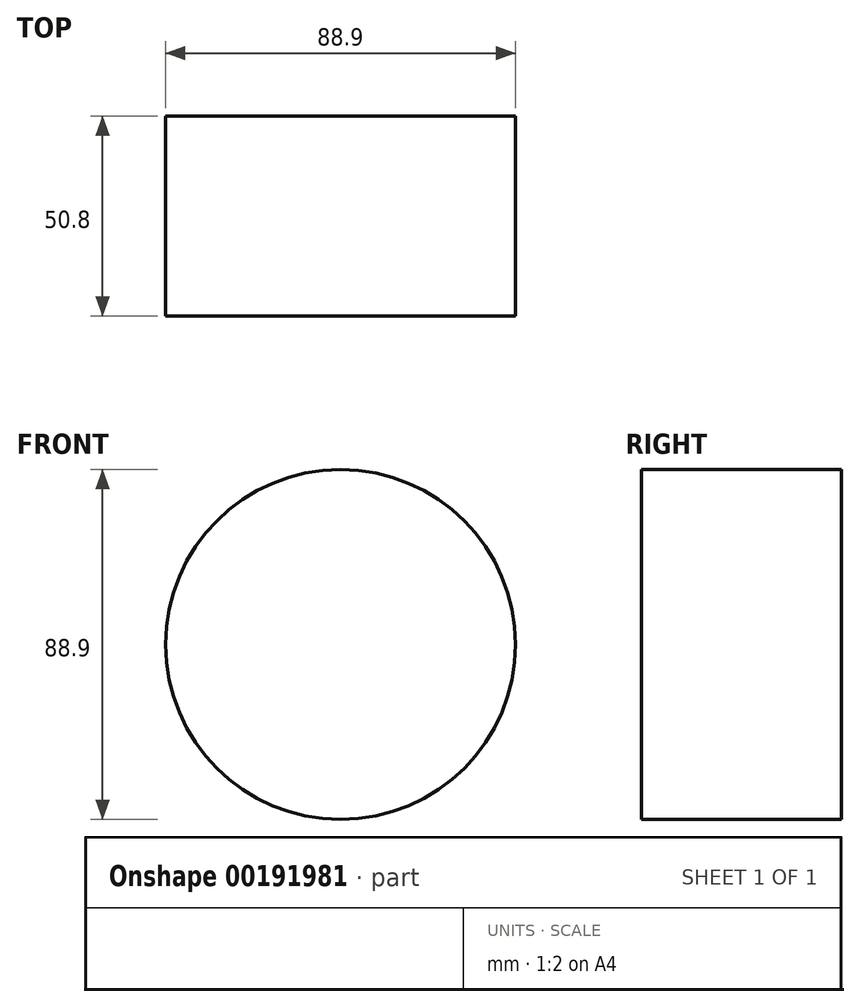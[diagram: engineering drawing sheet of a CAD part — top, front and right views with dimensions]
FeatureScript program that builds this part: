
annotation { "Feature Type Name" : "Feature", "Feature Type Description" : "" }
export const myFeature = defineFeature(function(context is Context, id is Id, definition is map)
    precondition{}
    {
        {
            var Q0;
            Q0=qCreatedBy(makeId("Front.planeOp"),FACE);
            var sketch = newSketch(context, id + "F0", { "sketchPlane" : qUnion([Q0])});
            skCircle(sketch, "E0", {"center": v(0, 0) * mm, "radius": 44.45 * mm});
            skSolve(sketch);
        }
        {
            var Q0;
            Q0=makeQuery(id+"F0.imprint","IMPRINT",FACE,{"disambiguationData":[TD([[makeQuery(id+"F0.imprint","IMPRINT",EDGE,{"derivedFrom":sQuery(id+"F0.wireOp",EDGE,"E0")}),1.0]])]});
            extrude(context, id + "F1", {"entities" : qUnion([Q0]), "depth" : 50.8 * mm});
        }
    });
